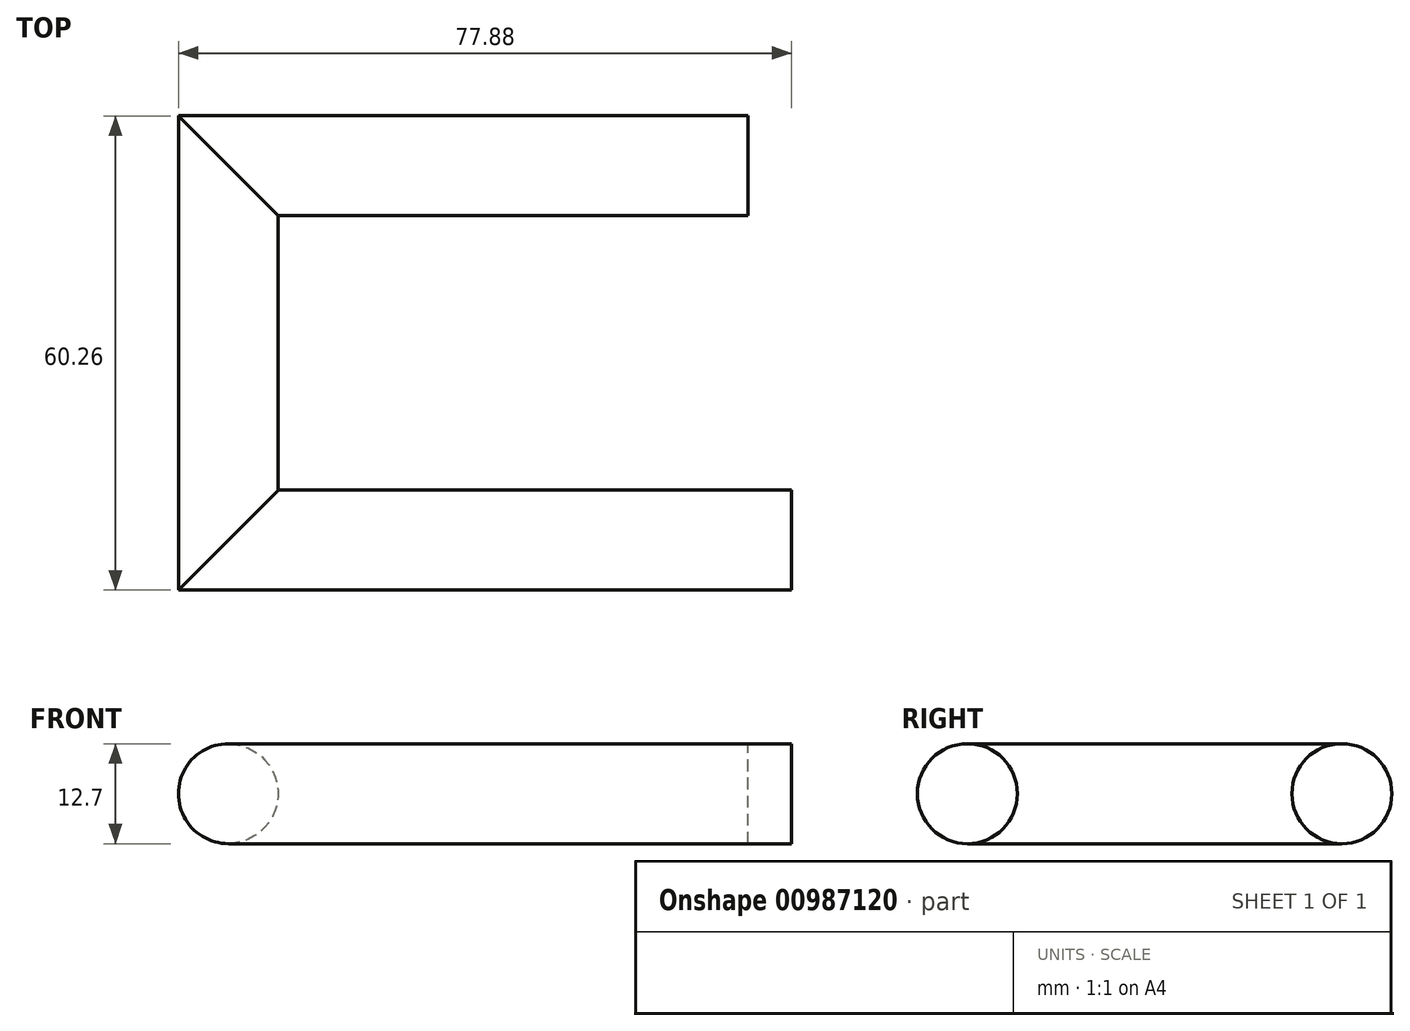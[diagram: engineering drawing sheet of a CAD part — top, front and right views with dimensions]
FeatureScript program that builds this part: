
annotation { "Feature Type Name" : "Feature", "Feature Type Description" : "" }
export const myFeature = defineFeature(function(context is Context, id is Id, definition is map)
    precondition{}
    {
        {
            var Q0;
            Q0=qCreatedBy(makeId("Top.planeOp"),FACE);
            var sketch = newSketch(context, id + "F0", { "sketchPlane" : qUnion([Q0])});
            skLineSegment(sketch, "E0", {"start": v(32.9, 23.87) * mm, "end": v(-33.1, 23.87) * mm});
            skLineSegment(sketch, "E1", {"start": v(-33.1, 23.87) * mm, "end": v(-33.1, -23.69) * mm});
            skLineSegment(sketch, "E2", {"start": v(-33.1, -23.69) * mm, "end": v(38.44, -23.69) * mm});
            skSolve(sketch);
        }
        {
            var Q0;
            Q0=sQuery(id+"F0.wireOp",VERTEX,"E2.end");
            var Q1;
            Q1=qCreatedBy(makeId("Right.planeOp"),FACE);
            cPlane(context, id + "F1", {"entities" : qUnion([Q0, Q1]), "cplaneType" : CPlaneType.PLANE_POINT, "offset" : 25.4 * mm, "width" : 152.4 * mm, "height" : 152.4 * mm});
        }
        {
            var Q0;
            Q0=qCreatedBy(id+"F1.planeOp",FACE);
            var sketch = newSketch(context, id + "F2", { "sketchPlane" : qUnion([Q0])});
            skCircle(sketch, "E3", {"center": v(-23.69, 0) * mm, "radius": 6.35 * mm});
            skSolve(sketch);
        }
        {
            var Q0;
            Q0=makeQuery(id+"F2.imprint","IMPRINT",FACE,{"disambiguationData":[TD([[makeQuery(id+"F2.imprint","IMPRINT",EDGE,{"derivedFrom":sQuery(id+"F2.wireOp",EDGE,"E3")}),1.0]])]});
            var Q1;
            Q1=sQuery(id+"F0.wireOp",EDGE,"E2");
            var Q2;
            Q2=sQuery(id+"F0.wireOp",EDGE,"E1");
            var Q3;
            Q3=sQuery(id+"F0.wireOp",EDGE,"E0");
            sweep(context, id + "F3", {"profiles" : qUnion([Q0]), "path" : qUnion([Q1, Q2, Q3])});
        }
    });
